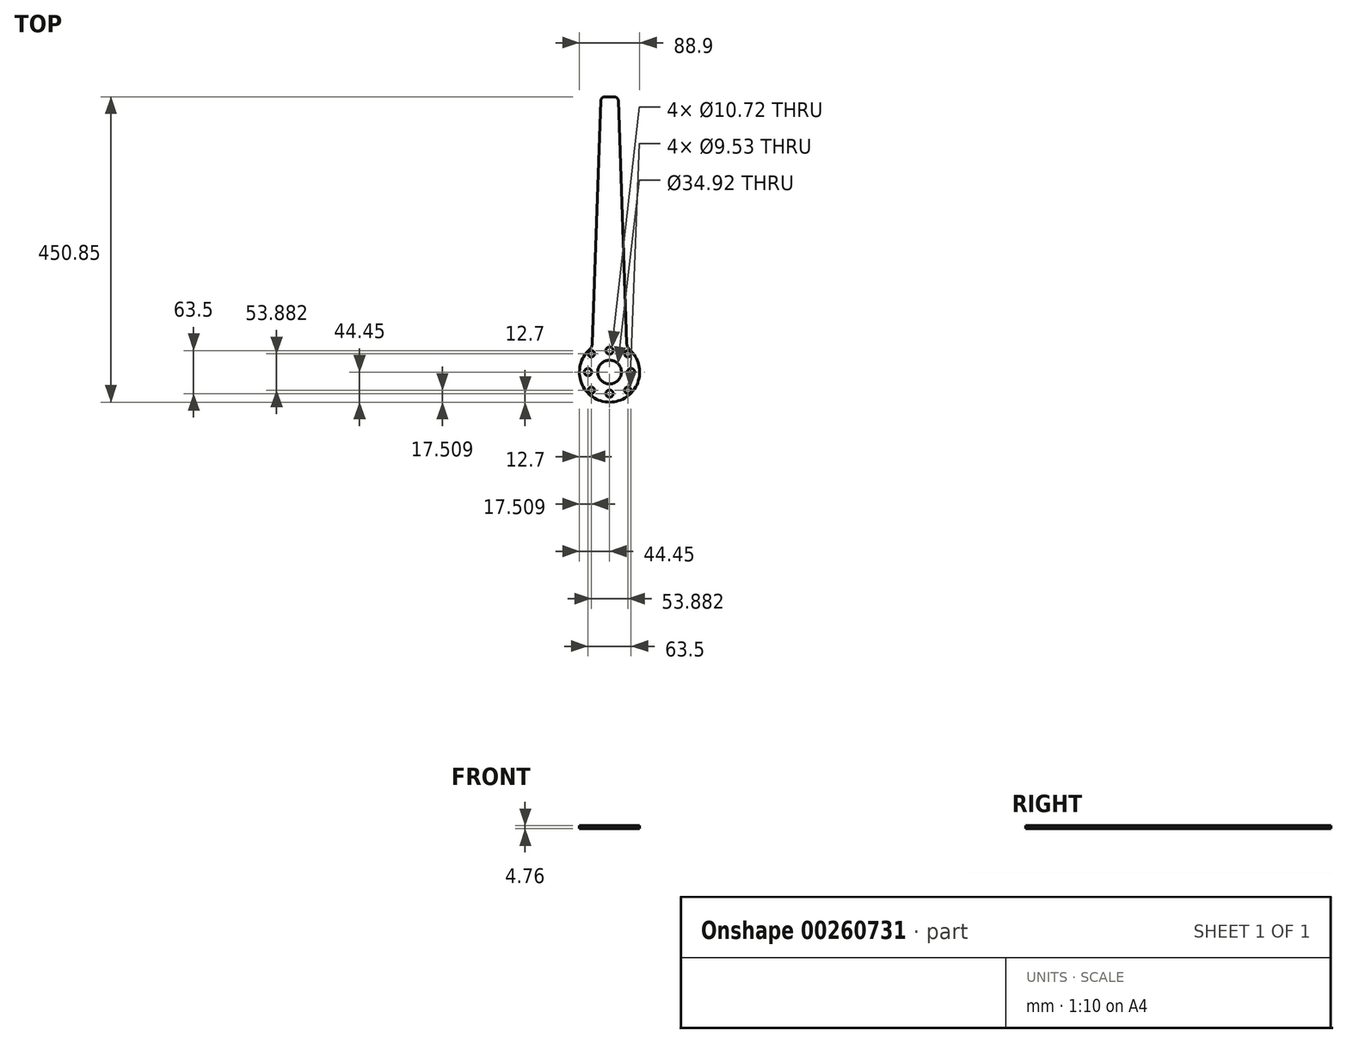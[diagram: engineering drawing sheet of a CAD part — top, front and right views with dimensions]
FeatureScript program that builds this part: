
annotation { "Feature Type Name" : "Feature", "Feature Type Description" : "" }
export const myFeature = defineFeature(function(context is Context, id is Id, definition is map)
    precondition{}
    {
        {
            var Q0;
            Q0=qCreatedBy(makeId("Top.planeOp"),FACE);
            var sketch = newSketch(context, id + "F0", { "sketchPlane" : qUnion([Q0])});
            skCircle(sketch, "E0", {"center": v(0, 0) * mm, "radius": 31.75 * mm, "construction": true});
            skArc(sketch, "E1", {"start": v(-29.63, 33.14) * mm, "mid": v(0, -44.45) * mm, "end": v(29.63, 33.14) * mm});
            skCircle(sketch, "E2", {"center": v(0, 0) * mm, "radius": 17.46 * mm});
            skLineSegment(sketch, "E3", {"start": v(-25.4, 42.16) * mm, "end": v(-12.7, 406.4) * mm});
            skLineSegment(sketch, "E4", {"start": v(25.4, 42.16) * mm, "end": v(12.7, 406.4) * mm});
            skLineSegment(sketch, "E5", {"start": v(-12.7, 406.4) * mm, "end": v(12.7, 406.4) * mm});
            skPoint(sketch, "E6.visualSharp", {"position": v(-25.6, 36.34) * mm});
            skArc(sketch, "E6.filletArc", {"start": v(-29.63, 33.14) * mm, "mid": v(-26.6, 37.22) * mm, "end": v(-25.4, 42.16) * mm});
            skPoint(sketch, "E7.visualSharp", {"position": v(25.6, 36.34) * mm});
            skArc(sketch, "E7.filletArc", {"start": v(25.4, 42.16) * mm, "mid": v(26.6, 37.22) * mm, "end": v(29.63, 33.14) * mm});
            skPoint(sketch, "E8", {"position": v(0, 31.75) * mm});
            skPoint(sketch, "E9.1.0", {"position": v(-31.75, 0) * mm});
            skPoint(sketch, "E9.2.0", {"position": v(0, -31.75) * mm});
            skPoint(sketch, "E9.3.0", {"position": v(31.75, 0) * mm});
            skSolve(sketch);
        }
        {
            var Q0;
            Q0=makeQuery(id+"F0.imprint","IMPRINT",FACE,{"disambiguationData":[TD([[makeQuery(id+"F0.imprint","IMPRINT",EDGE,{"derivedFrom":sQuery(id+"F0.wireOp",EDGE,"E1")}),1.0]])]});
            extrude(context, id + "F1", {"entities" : qUnion([Q0]), "oppositeDirection" : true, "depth" : 4.76 * mm});
        }
        {
            var Q0;
            Q0=sQuery(id+"F0.wireOp",VERTEX,"E8");
            var Q1;
            Q1=sQuery(id+"F0.wireOp",VERTEX,"E9.3.0");
            var Q2;
            Q2=sQuery(id+"F0.wireOp",VERTEX,"E9.2.0");
            var Q3;
            Q3=sQuery(id+"F0.wireOp",VERTEX,"E9.1.0");
            var Q4;
            Q4=makeQuery(id+"F1.opExtrude","SWEPT_BODY",BODY,{"disambiguationData":[OSD([sQuery(id+"F0.wireOp",EDGE,"E1"),sQuery(id+"F0.wireOp",EDGE,"E2"),sQuery(id+"F0.wireOp",EDGE,"E3"),sQuery(id+"F0.wireOp",EDGE,"E4"),sQuery(id+"F0.wireOp",EDGE,"E5"),sQuery(id+"F0.wireOp",EDGE,"E6.filletArc"),sQuery(id+"F0.wireOp",EDGE,"E7.filletArc")])]});
            hole(context, id + "F2", {"style" : HoleStyle.SIMPLE, "endStyle" : HoleEndStyle.THROUGH, "holeDiameter" : 10.72 * mm, "tappedDepth" : 12.7 * mm, "tapClearance" : 3, "locations" : qUnion([Q0, Q1, Q2, Q3]), "scope" : qUnion([Q4])});
        }
        {
            var Q0;
            Q0=makeQuery(id+"F1.opExtrude","SWEPT_EDGE",EDGE,{"disambiguationData":[OSD([sQuery(id+"F0.wireOp",EDGE,"E3"),sQuery(id+"F0.wireOp",EDGE,"E5")])]});
            var Q1;
            Q1=makeQuery(id+"F1.opExtrude","SWEPT_EDGE",EDGE,{"disambiguationData":[OSD([sQuery(id+"F0.wireOp",EDGE,"E4"),sQuery(id+"F0.wireOp",EDGE,"E5")])]});
            fillet(context, id + "F3", {"entities" : qUnion([Q0, Q1]), "radius" : 6.35 * mm, "tangentPropagation" : true, "allowEdgeOverflow" : false});
        }
        {
            var Q0;
            Q0=makeQuery(id+"F1.opExtrude","CAP_FACE",FACE,{"disambiguationData":[OSD([sQuery(id+"F0.wireOp",EDGE,"E1"),sQuery(id+"F0.wireOp",EDGE,"E2"),sQuery(id+"F0.wireOp",EDGE,"E3"),sQuery(id+"F0.wireOp",EDGE,"E4"),sQuery(id+"F0.wireOp",EDGE,"E5"),sQuery(id+"F0.wireOp",EDGE,"E6.filletArc"),sQuery(id+"F0.wireOp",EDGE,"E7.filletArc")])],"isStart":true});
            var sketch = newSketch(context, id + "F4", { "sketchPlane" : qUnion([Q0])});
            skCircle(sketch, "E10", {"center": v(0, 0) * mm, "radius": 38.1 * mm});
            skPoint(sketch, "E11", {"position": v(-26.94, 26.94) * mm});
            skLineSegment(sketch, "E12", {"start": v(0, 0) * mm, "end": v(-26.94, 26.94) * mm});
            skLineSegment(sketch, "E13", {"start": v(0, 0) * mm, "end": v(0, 118.86) * mm});
            skPoint(sketch, "E14.1.0", {"position": v(-26.94, -26.94) * mm});
            skPoint(sketch, "E14.2.0", {"position": v(26.94, -26.94) * mm});
            skPoint(sketch, "E15.0.3.0", {"position": v(26.94, 26.94) * mm});
            skSolve(sketch);
        }
        {
            var Q0;
            Q0=sQuery(id+"F4.wireOp",VERTEX,"E12.end");
            var Q1;
            Q1=sQuery(id+"F4.wireOp",VERTEX,"E15.0.3.0");
            var Q2;
            Q2=sQuery(id+"F4.wireOp",VERTEX,"E14.2.0");
            var Q3;
            Q3=sQuery(id+"F4.wireOp",VERTEX,"E14.1.0");
            var Q4;
            Q4=makeQuery(id+"F1.opExtrude","SWEPT_BODY",BODY,{"disambiguationData":[OSD([sQuery(id+"F0.wireOp",EDGE,"E1"),sQuery(id+"F0.wireOp",EDGE,"E2"),sQuery(id+"F0.wireOp",EDGE,"E3"),sQuery(id+"F0.wireOp",EDGE,"E4"),sQuery(id+"F0.wireOp",EDGE,"E5"),sQuery(id+"F0.wireOp",EDGE,"E6.filletArc"),sQuery(id+"F0.wireOp",EDGE,"E7.filletArc")])]});
            hole(context, id + "F5", {"style" : HoleStyle.SIMPLE, "endStyle" : HoleEndStyle.THROUGH, "holeDiameter" : 9.52 * mm, "isTappedThrough" : true, "tappedDepth" : 12.7 * mm, "tapClearance" : 3, "locations" : qUnion([Q0, Q1, Q2, Q3]), "scope" : qUnion([Q4])});
        }
    });
